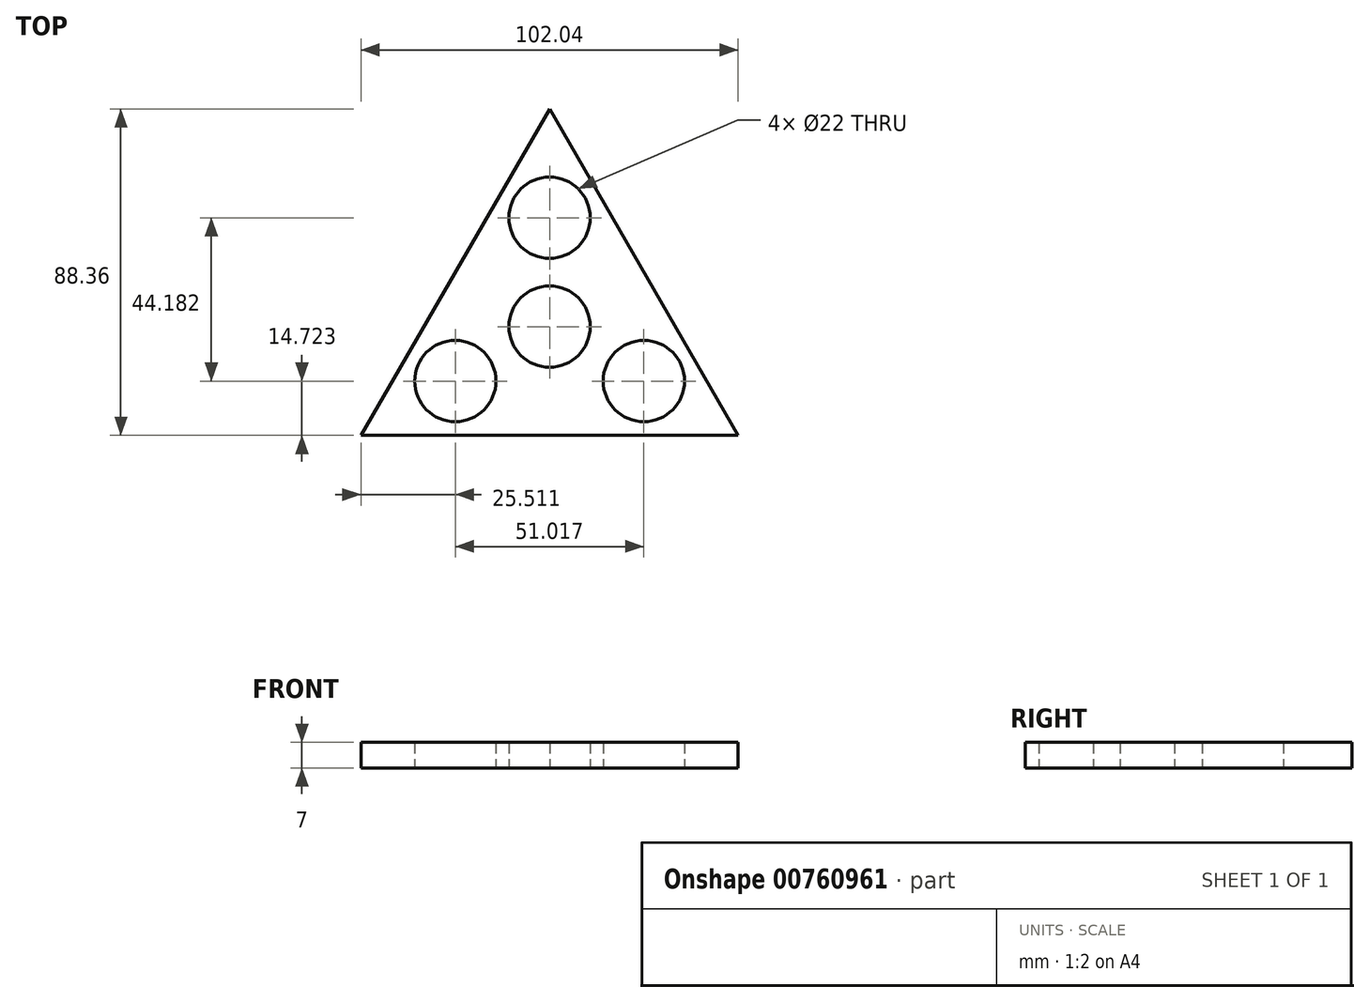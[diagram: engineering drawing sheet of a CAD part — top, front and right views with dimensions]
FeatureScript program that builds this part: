
annotation { "Feature Type Name" : "Feature", "Feature Type Description" : "" }
export const myFeature = defineFeature(function(context is Context, id is Id, definition is map)
    precondition{}
    {
        {
            var Q0;
            Q0=qCreatedBy(makeId("Top.planeOp"),FACE);
            var sketch = newSketch(context, id + "F0", { "sketchPlane" : qUnion([Q0])});
            skCircle(sketch, "E0", {"center": v(0, 0) * mm, "radius": 11 * mm});
            skCircle(sketch, "E1.cCircle", {"center": v(0, 0) * mm, "radius": 29.45 * mm, "construction": true});
            skLineSegment(sketch, "E1.0", {"start": v(51.02, -29.45) * mm, "end": v(-51.02, -29.45) * mm});
            skLineSegment(sketch, "E1.1", {"start": v(-51.02, -29.45) * mm, "end": v(0, 58.9) * mm});
            skLineSegment(sketch, "E1.2", {"start": v(0, 58.9) * mm, "end": v(51.02, -29.45) * mm});
            skPoint(sketch, "E1.0.midPoint", {"position": v(0, -29.45) * mm});
            skCircle(sketch, "E2", {"center": v(-25.5, -14.73) * mm, "radius": 11 * mm});
            skCircle(sketch, "E3", {"center": v(25.5, -14.73) * mm, "radius": 11 * mm});
            skCircle(sketch, "E4", {"center": v(0, 29.45) * mm, "radius": 11 * mm});
            skSolve(sketch);
        }
        {
            var Q0;
            Q0=makeQuery(id+"F0.imprint","IMPRINT",FACE,{"disambiguationData":[TD([[makeQuery(id+"F0.imprint","IMPRINT",EDGE,{"derivedFrom":sQuery(id+"F0.wireOp",EDGE,"E0")}),-1.0]])]});
            extrude(context, id + "F1", {"entities" : qUnion([Q0]), "depth" : 7 * mm, "offsetDistance" : 25 * mm});
        }
    });
